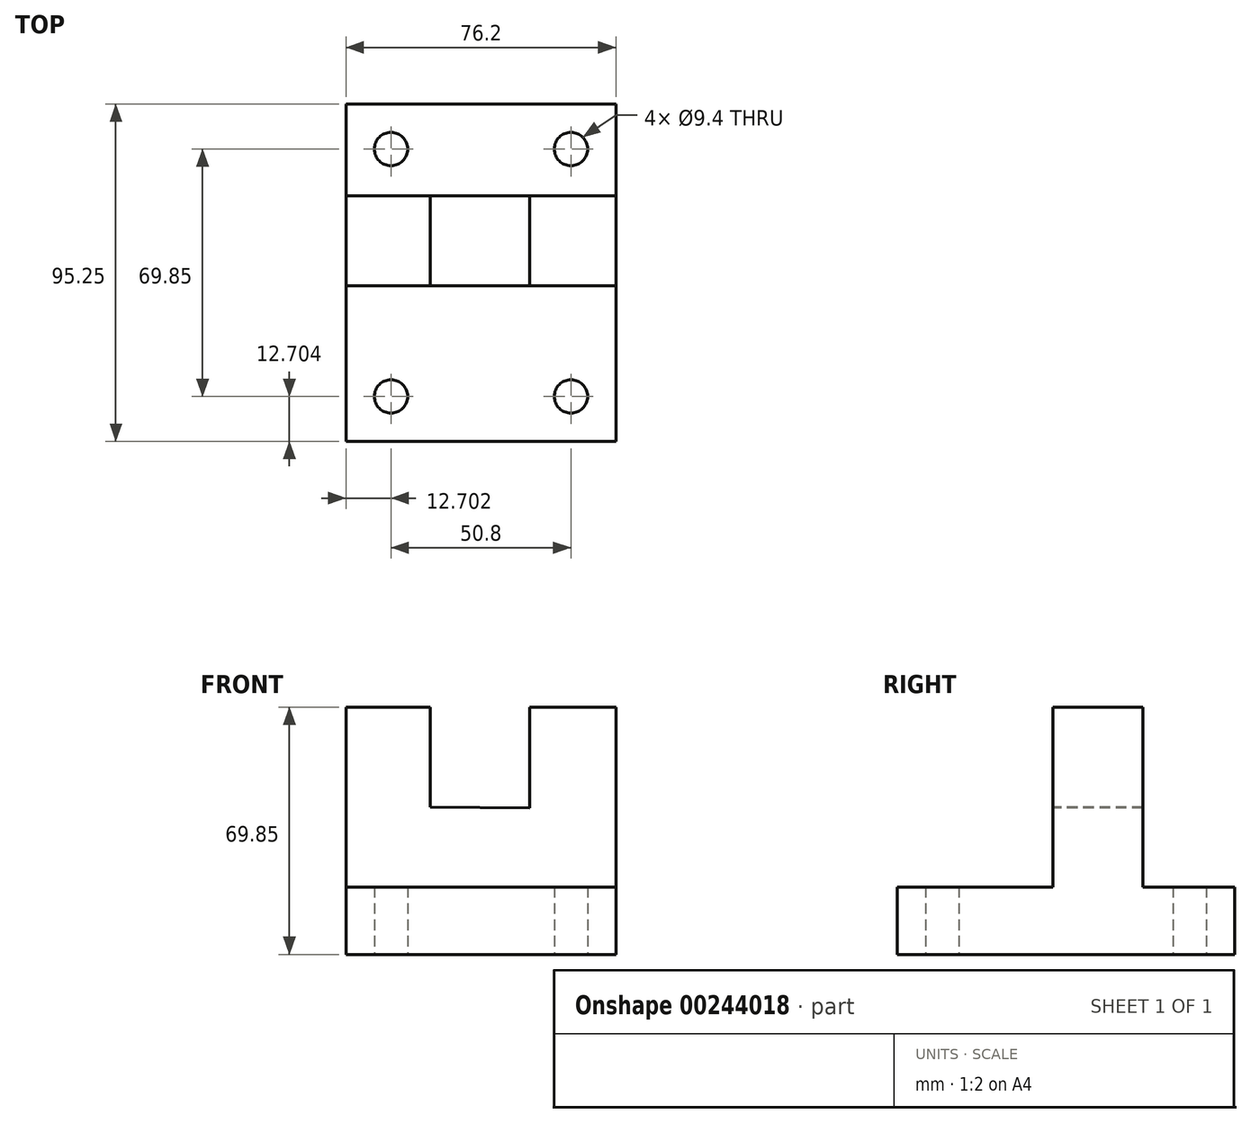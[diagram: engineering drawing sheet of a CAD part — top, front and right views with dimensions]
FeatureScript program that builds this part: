
annotation { "Feature Type Name" : "Feature", "Feature Type Description" : "" }
export const myFeature = defineFeature(function(context is Context, id is Id, definition is map)
    precondition{}
    {
        {
            var Q0;
            Q0=qCreatedBy(makeId("Top.planeOp"),FACE);
            var sketch = newSketch(context, id + "F0", { "sketchPlane" : qUnion([Q0])});
            skLineSegment(sketch, "E0.bottom", {"start": v(-28.23, 48.8) * mm, "end": v(47.97, 48.8) * mm});
            skLineSegment(sketch, "E0.top", {"start": v(-28.23, -46.45) * mm, "end": v(47.97, -46.45) * mm});
            skLineSegment(sketch, "E0.left", {"start": v(-28.23, 48.8) * mm, "end": v(-28.23, -46.45) * mm});
            skLineSegment(sketch, "E0.right", {"start": v(47.97, 48.8) * mm, "end": v(47.97, -46.45) * mm});
            skSolve(sketch);
        }
        {
            var Q0;
            Q0 = qSketchRegion(id + "F0", true);
            extrude(context, id + "F1", {"entities" : qUnion([Q0]), "depth" : 69.85 * mm});
        }
        {
            var Q0;
            Q0=qCreatedBy(makeId("Front.planeOp"),FACE);
            var sketch = newSketch(context, id + "F2", { "sketchPlane" : qUnion([Q0])});
            skLineSegment(sketch, "E1", {"start": v(23.56, 69.94) * mm, "end": v(23.56, 41.36) * mm});
            skPoint(sketch, "E2.orphan", {"position": v(23.56, 0) * mm});
            skLineSegment(sketch, "E3", {"start": v(-4.5, 70.18) * mm, "end": v(-4.5, 41.6) * mm});
            skLineSegment(sketch, "E4", {"start": v(-4.5, 41.6) * mm, "end": v(23.56, 41.36) * mm});
            skLineSegment(sketch, "E5", {"start": v(-4.5, 70.18) * mm, "end": v(23.56, 69.94) * mm});
            skSolve(sketch);
        }
        {
            var Q0;
            Q0 = qSketchRegion(id + "F2", true);
            extrude(context, id + "F3", {"entities" : qUnion([Q0]), "operationType" : NewBodyOperationType.REMOVE, "endBound" : BoundingType.SYMMETRIC, "oppositeDirection" : true, "depth" : 102.62 * mm});
        }
        {
            var Q0;
            Q0=qCreatedBy(makeId("Right.planeOp"),FACE);
            var sketch = newSketch(context, id + "F4", { "sketchPlane" : qUnion([Q0])});
            skLineSegment(sketch, "E6", {"start": v(-46.96, 19.05) * mm, "end": v(-2.5, 19.05) * mm});
            skLineSegment(sketch, "E7", {"start": v(-2.5, 19.05) * mm, "end": v(-2.5, 69.84) * mm});
            skLineSegment(sketch, "E8", {"start": v(22.9, 69.84) * mm, "end": v(22.9, 19.05) * mm});
            skLineSegment(sketch, "E9", {"start": v(22.9, 19.05) * mm, "end": v(48.3, 19.05) * mm});
            skLineSegment(sketch, "E10", {"start": v(-46.96, 69.84) * mm, "end": v(-46.96, 19.05) * mm});
            skLineSegment(sketch, "E11", {"start": v(-46.96, 69.84) * mm, "end": v(-2.5, 69.84) * mm});
            skPoint(sketch, "E12.start.orphan", {"position": v(-46.96, 0) * mm});
            skPoint(sketch, "E13.end.orphan", {"position": v(48.3, 0) * mm});
            skPoint(sketch, "E14.end.orphan", {"position": v(48.3, 69.84) * mm});
            skLineSegment(sketch, "E15", {"start": v(22.9, 69.84) * mm, "end": v(51.4, 69.84) * mm});
            skLineSegment(sketch, "E16", {"start": v(51.4, 69.84) * mm, "end": v(51.4, 19.05) * mm});
            skLineSegment(sketch, "E17", {"start": v(51.4, 19.05) * mm, "end": v(48.3, 19.05) * mm});
            skLineSegment(sketch, "E18", {"start": v(-2.5, 69.84) * mm, "end": v(-2.5, 73.23) * mm});
            skLineSegment(sketch, "E19", {"start": v(-2.5, 73.23) * mm, "end": v(-46.96, 73.23) * mm});
            skLineSegment(sketch, "E20", {"start": v(-46.96, 73.23) * mm, "end": v(-46.96, 69.84) * mm});
            skLineSegment(sketch, "E21", {"start": v(-46.96, 73.23) * mm, "end": v(-52.01, 73.23) * mm});
            skLineSegment(sketch, "E22", {"start": v(-52.01, 73.23) * mm, "end": v(-52.01, 19.05) * mm});
            skLineSegment(sketch, "E23", {"start": v(-52.01, 19.05) * mm, "end": v(-46.96, 19.05) * mm});
            skLineSegment(sketch, "E24", {"start": v(51.4, 69.84) * mm, "end": v(51.4, 73.23) * mm});
            skLineSegment(sketch, "E25", {"start": v(51.4, 73.23) * mm, "end": v(22.9, 73.23) * mm});
            skLineSegment(sketch, "E26", {"start": v(22.9, 73.23) * mm, "end": v(22.9, 69.84) * mm});
            skSolve(sketch);
        }
        {
            var Q0;
            Q0 = qSketchRegion(id + "F4", true);
            extrude(context, id + "F5", {"entities" : qUnion([Q0]), "operationType" : NewBodyOperationType.REMOVE, "endBound" : BoundingType.SYMMETRIC, "oppositeDirection" : true, "depth" : 266.7 * mm});
        }
        {
            var Q0;
            Q0=qCreatedBy(makeId("Top.planeOp"),FACE);
            var sketch = newSketch(context, id + "F6", { "sketchPlane" : qUnion([Q0])});
            skCircle(sketch, "E27", {"center": v(-15.53, 36.1) * mm, "radius": 4.7 * mm});
            skPoint(sketch, "E28.0", {"position": v(9.87, 48.8) * mm});
            skCircle(sketch, "E29.MirrorC", {"center": v(35.27, 36.1) * mm, "radius": 4.7 * mm});
            skCircle(sketch, "E30", {"center": v(-15.53, -33.75) * mm, "radius": 4.7 * mm});
            skPoint(sketch, "E31.0", {"position": v(9.87, -46.45) * mm});
            skLineSegment(sketch, "E32.0", {"start": v(47.97, -46.45) * mm, "end": v(-28.23, -46.45) * mm, "construction": true});
            skLineSegment(sketch, "E32.1", {"start": v(-28.23, -46.45) * mm, "end": v(47.97, -46.45) * mm, "construction": true});
            skLineSegment(sketch, "E33", {"start": v(9.87, -46.45) * mm, "end": v(9.87, -16.95) * mm, "construction": true});
            skCircle(sketch, "E34.MirrorC", {"center": v(35.27, -33.75) * mm, "radius": 4.7 * mm});
            skSolve(sketch);
        }
        {
            var Q0;
            Q0 = qSketchRegion(id + "F6", true);
            extrude(context, id + "F7", {"entities" : qUnion([Q0]), "operationType" : NewBodyOperationType.REMOVE, "depth" : 164.85 * mm});
        }
    });
